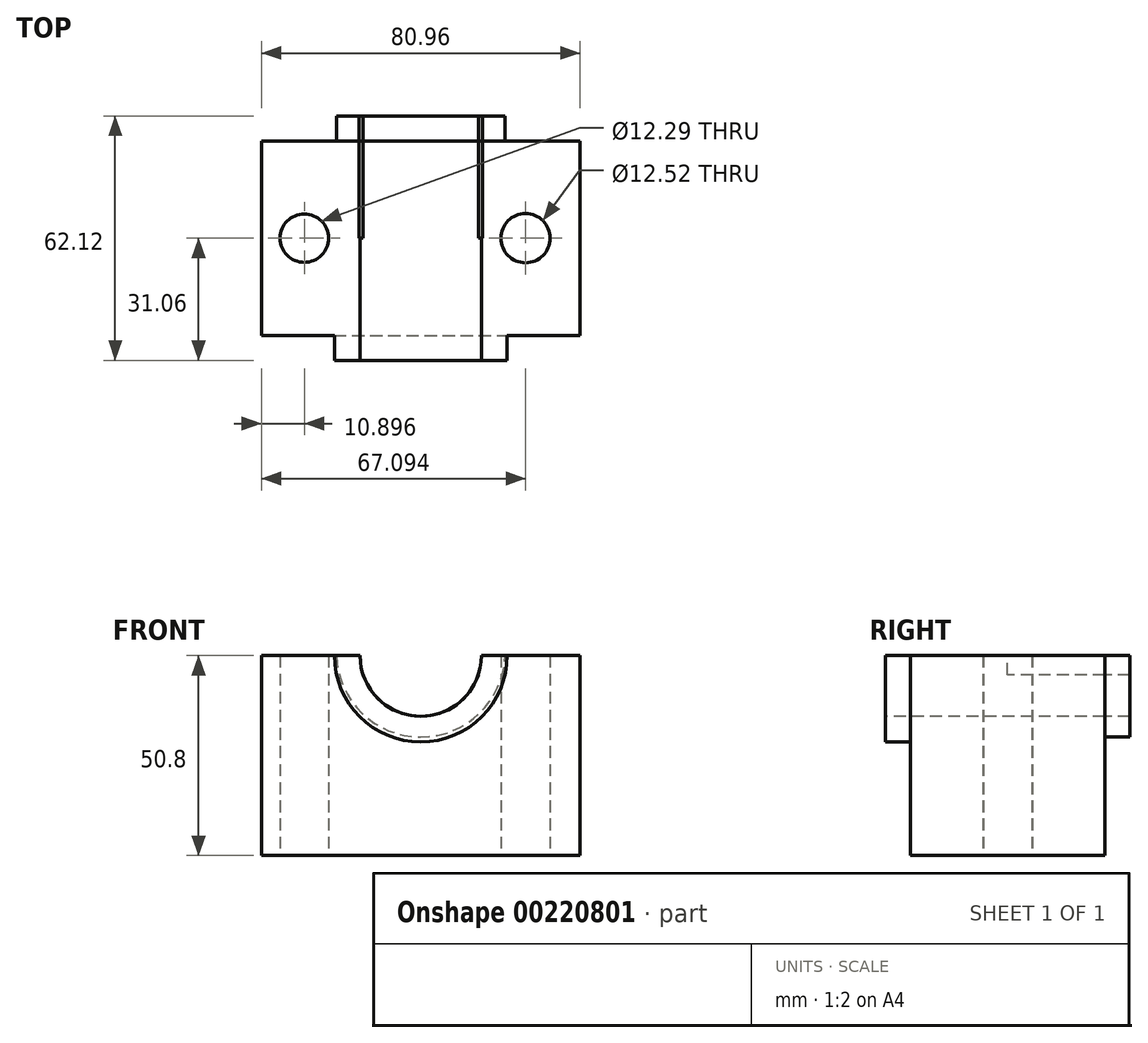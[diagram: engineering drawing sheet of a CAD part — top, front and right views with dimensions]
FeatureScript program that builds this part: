
annotation { "Feature Type Name" : "Feature", "Feature Type Description" : "" }
export const myFeature = defineFeature(function(context is Context, id is Id, definition is map)
    precondition{}
    {
        {
            var Q0;
            Q0=qCreatedBy(makeId("Top.planeOp"),FACE);
            var sketch = newSketch(context, id + "F0", { "sketchPlane" : qUnion([Q0])});
            skLineSegment(sketch, "E0.bottom", {"start": v(-40.48, -24.7) * mm, "end": v(40.48, -24.7) * mm});
            skLineSegment(sketch, "E0.top", {"start": v(-40.48, 24.7) * mm, "end": v(40.48, 24.7) * mm});
            skLineSegment(sketch, "E0.left", {"start": v(-40.48, -24.7) * mm, "end": v(-40.48, 24.7) * mm});
            skLineSegment(sketch, "E0.right", {"start": v(40.48, -24.7) * mm, "end": v(40.48, 24.7) * mm});
            skPoint(sketch, "E0.middle", {"position": v(0, 0) * mm});
            skCircle(sketch, "E1", {"center": v(-29.58, 0) * mm, "radius": 6.14 * mm});
            skCircle(sketch, "E2", {"center": v(26.61, 0) * mm, "radius": 6.26 * mm});
            skSolve(sketch);
        }
        {
            var Q0;
            Q0 = qSketchRegion(id + "F0", true);
            extrude(context, id + "F1", {"entities" : qUnion([Q0]), "depth" : 50.8 * mm});
        }
        {
            var Q0;
            Q0=qCreatedBy(makeId("Front.planeOp"),FACE);
            var sketch = newSketch(context, id + "F2", { "sketchPlane" : qUnion([Q0])});
            skArc(sketch, "E3", {"start": v(-15.67, 50.8) * mm, "mid": v(0, 35.89) * mm, "end": v(15.67, 50.8) * mm});
            skLineSegment(sketch, "E4", {"start": v(-15.67, 50.8) * mm, "end": v(15.67, 50.8) * mm});
            skSolve(sketch);
        }
        {
            var Q0;
            Q0=makeQuery(id+"F2.imprint","IMPRINT",FACE,{"disambiguationData":[TD([[makeQuery(id+"F2.imprint","IMPRINT",EDGE,{"derivedFrom":sQuery(id+"F2.wireOp",EDGE,"E3")}),1.0]])]});
            var Q1;
            Q1=makeQuery(id+"F1.opExtrude","SWEPT_BODY",BODY,{"disambiguationData":[OSD([sQuery(id+"F0.wireOp",EDGE,"E0.bottom"),sQuery(id+"F0.wireOp",EDGE,"E0.top"),sQuery(id+"F0.wireOp",EDGE,"E0.left"),sQuery(id+"F0.wireOp",EDGE,"E0.right"),sQuery(id+"F0.wireOp",EDGE,"E1"),sQuery(id+"F0.wireOp",EDGE,"E2")])]});
            extrude(context, id + "F3", {"entities" : qUnion([Q0]), "operationType" : NewBodyOperationType.REMOVE, "endBound" : BoundingType.UP_TO_BODY, "oppositeDirection" : true, "endBoundEntityBody" : qUnion([Q1]), "depth" : 25.4 * mm});
        }
        {
            var Q0;
            Q0=makeQuery(id+"F1.opExtrude","SWEPT_FACE",FACE,{"disambiguationData":[OSD([sQuery(id+"F0.wireOp",EDGE,"E0.bottom")])]});
            var sketch = newSketch(context, id + "F4", { "sketchPlane" : qUnion([Q0])});
            skLineSegment(sketch, "E5", {"start": v(-15.42, 50.8) * mm, "end": v(15.42, 50.8) * mm});
            skLineSegment(sketch, "E6", {"start": v(15.42, 50.8) * mm, "end": v(-15.6, 50.8) * mm});
            skArc(sketch, "E7", {"start": v(-15.42, 50.8) * mm, "mid": v(0, 35.38) * mm, "end": v(15.42, 50.8) * mm});
            skSolve(sketch);
        }
        {
            var Q0;
            {var subQ0=sQuery(id+"F4.wireOp",EDGE,"E7");Q0=makeQuery(id+"F4.imprint","IMPRINT",FACE,{"disambiguationData":[TD([[makeQuery(id+"F4.imprint","IMPRINT",EDGE,{"derivedFrom":subQ0}),1.0]])]});}
            extrude(context, id + "F5", {"entities" : qUnion([Q0]), "operationType" : NewBodyOperationType.REMOVE, "endBound" : BoundingType.THROUGH_ALL, "oppositeDirection" : true, "depth" : 25.4 * mm});
        }
        {
            var Q0;
            Q0=makeQuery(id+"F1.opExtrude","SWEPT_FACE",FACE,{"disambiguationData":[OSD([sQuery(id+"F0.wireOp",EDGE,"E0.top")])]});
            var sketch = newSketch(context, id + "F6", { "sketchPlane" : qUnion([Q0])});
            skLineSegment(sketch, "E8", {"start": v(-15.67, 50.8) * mm, "end": v(-21.45, 50.8) * mm});
            skLineSegment(sketch, "E9", {"start": v(15.67, 50.8) * mm, "end": v(21.93, 50.8) * mm});
            skArc(sketch, "E10", {"start": v(-21.45, 50.8) * mm, "mid": v(0, 30.11) * mm, "end": v(21.45, 50.8) * mm});
            skArc(sketch, "E11", {"start": v(15.67, 50.8) * mm, "mid": v(0, 35.89) * mm, "end": v(-15.67, 50.8) * mm});
            skSolve(sketch);
        }
        {
            var Q0;
            {var subQ1=sQuery(id+"F6.wireOp",EDGE,"E8");Q0=makeQuery(id+"F6.imprint","IMPRINT",FACE,{"disambiguationData":[TD([[makeQuery(id+"F6.imprint","IMPRINT",EDGE,{"derivedFrom":subQ1}),1.0]])]});}
            extrude(context, id + "F7", {"entities" : qUnion([Q0]), "depth" : 6.35 * mm});
        }
        {
            var Q0;
            Q0=makeQuery(id+"F1.opExtrude","SWEPT_FACE",FACE,{"disambiguationData":[OSD([sQuery(id+"F0.wireOp",EDGE,"E0.bottom")])]});
            var sketch = newSketch(context, id + "F8", { "sketchPlane" : qUnion([Q0])});
            skLineSegment(sketch, "E12", {"start": v(-15.42, 50.8) * mm, "end": v(-21.93, 50.8) * mm});
            skLineSegment(sketch, "E13", {"start": v(15.42, 50.8) * mm, "end": v(21.93, 50.8) * mm});
            skArc(sketch, "E14", {"start": v(-15.42, 50.8) * mm, "mid": v(0, 35.38) * mm, "end": v(15.42, 50.8) * mm});
            skArc(sketch, "E15", {"start": v(-21.93, 50.8) * mm, "mid": v(0, 28.87) * mm, "end": v(21.93, 50.8) * mm});
            skSolve(sketch);
        }
        {
            var Q0;
            Q0 = qSketchRegion(id + "F8", true);
            extrude(context, id + "F9", {"entities" : qUnion([Q0]), "operationType" : NewBodyOperationType.ADD, "depth" : 6.35 * mm});
        }
    });
